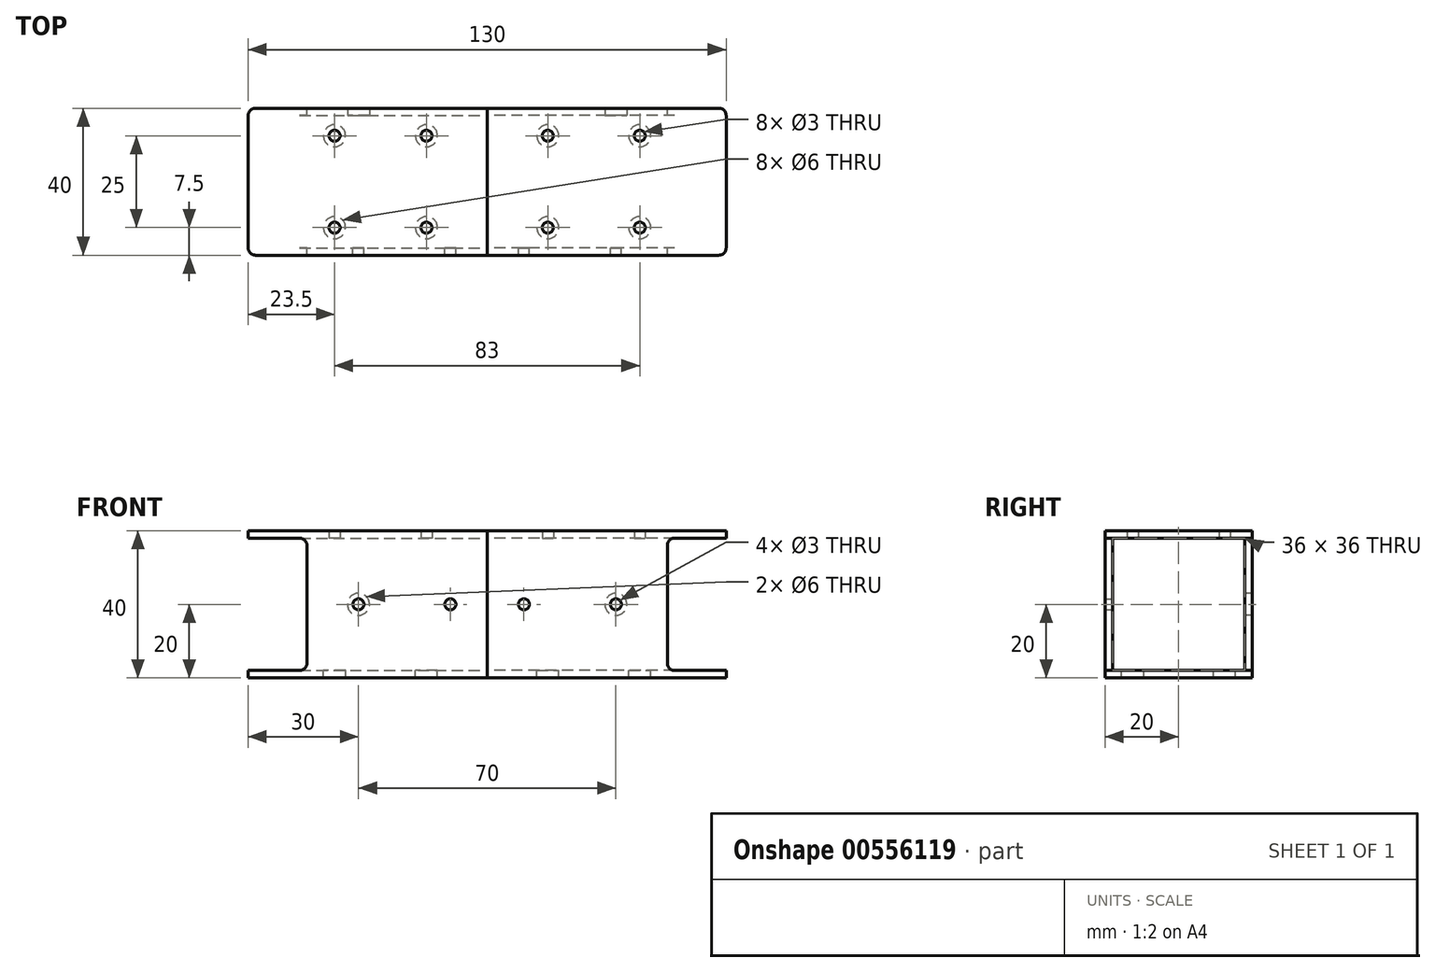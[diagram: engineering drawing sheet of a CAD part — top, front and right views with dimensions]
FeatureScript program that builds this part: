
annotation { "Feature Type Name" : "Feature", "Feature Type Description" : "" }
export const myFeature = defineFeature(function(context is Context, id is Id, definition is map)
    precondition{}
    {
        {
            var Q0;
            Q0=qCreatedBy(makeId("Right.planeOp"),FACE);
            var sketch = newSketch(context, id + "F0", { "sketchPlane" : qUnion([Q0])});
            skLineSegment(sketch, "E0.bottom", {"start": v(20, 20) * mm, "end": v(-20, 20) * mm});
            skLineSegment(sketch, "E0.top", {"start": v(20, -20) * mm, "end": v(-20, -20) * mm});
            skLineSegment(sketch, "E0.left", {"start": v(20, 20) * mm, "end": v(20, -20) * mm});
            skLineSegment(sketch, "E0.right", {"start": v(-20, 20) * mm, "end": v(-20, -20) * mm});
            skPoint(sketch, "E0.middle", {"position": v(0, 0) * mm});
            skSolve(sketch);
        }
        {
            var Q0;
            Q0=qSketchRegion(id+"F0",true);
            extrude(context, id + "F1", {"entities" : qUnion([Q0]), "oppositeDirection" : true, "depth" : 65 * mm, "offsetDistance" : 25 * mm});
        }
        {
            var Q0;
            Q0=makeQuery(id+"F1.opExtrude","CAP_FACE",FACE,{"disambiguationData":[OSD([sQuery(id+"F0.wireOp",EDGE,"E0.bottom"),sQuery(id+"F0.wireOp",EDGE,"E0.top"),sQuery(id+"F0.wireOp",EDGE,"E0.left"),sQuery(id+"F0.wireOp",EDGE,"E0.right")])],"isStart":false});
            var Q1;
            Q1=makeQuery(id+"F1.opExtrude","CAP_FACE",FACE,{"disambiguationData":[OSD([sQuery(id+"F0.wireOp",EDGE,"E0.bottom"),sQuery(id+"F0.wireOp",EDGE,"E0.top"),sQuery(id+"F0.wireOp",EDGE,"E0.left"),sQuery(id+"F0.wireOp",EDGE,"E0.right")])],"isStart":true});
            shell(context, id + "F2", {"entities" : qUnion([Q0, Q1]), "thickness" : 2 * mm});
        }
        {
            var Q0;
            Q0=makeQuery(id+"F2.opShell","OFFSET_FACE",FACE,{"disambiguationData":[OSD([sQuery(id+"F0.wireOp",EDGE,"E0.top")])]});
            var sketch = newSketch(context, id + "F3", { "sketchPlane" : qUnion([Q0])});
            skLineSegment(sketch, "E1", {"start": v(-65, 0) * mm, "end": v(0, 0) * mm, "construction": true});
            skLineSegment(sketch, "E2.bottom", {"start": v(-16.5, 12.5) * mm, "end": v(-41.5, 12.5) * mm, "construction": true});
            skLineSegment(sketch, "E2.top", {"start": v(-16.5, -12.5) * mm, "end": v(-41.5, -12.5) * mm, "construction": true});
            skLineSegment(sketch, "E2.left", {"start": v(-16.5, 12.5) * mm, "end": v(-16.5, -12.5) * mm, "construction": true});
            skLineSegment(sketch, "E2.right", {"start": v(-41.5, 12.5) * mm, "end": v(-41.5, -12.5) * mm, "construction": true});
            skPoint(sketch, "E2.middle", {"position": v(-29, 0) * mm});
            skLineSegment(sketch, "E3", {"start": v(-45, 18) * mm, "end": v(-45, -18) * mm, "construction": true});
            skSolve(sketch);
        }
        {
            var Q0;
            Q0=sQuery(id+"F3.wireOp",VERTEX,"E2.right.start");
            var Q1;
            Q1=sQuery(id+"F3.wireOp",VERTEX,"E2.bottom.start");
            var Q2;
            Q2=sQuery(id+"F3.wireOp",VERTEX,"E2.top.end");
            var Q3;
            Q3=sQuery(id+"F3.wireOp",VERTEX,"E2.left.end");
            var Q4;
            Q4=makeQuery(id+"F1.opExtrude","SWEPT_BODY",BODY,{"disambiguationData":[OSD([sQuery(id+"F0.wireOp",EDGE,"E0.bottom"),sQuery(id+"F0.wireOp",EDGE,"E0.top"),sQuery(id+"F0.wireOp",EDGE,"E0.left"),sQuery(id+"F0.wireOp",EDGE,"E0.right")])]});
            hole(context, id + "F4", {"style" : HoleStyle.SIMPLE, "endStyle" : HoleEndStyle.BLIND, "oppositeDirection" : true, "holeDiameter" : 3 * mm, "majorDiameter" : 5 * mm, "holeDepth" : 40 * mm, "isTappedThrough" : true, "tappedDepth" : 12 * mm, "tapClearance" : 3, "locations" : qUnion([Q0, Q1, Q2, Q3]), "scope" : qUnion([Q4])});
        }
        {
            var Q0;
            Q0=sQuery(id+"F3.wireOp",VERTEX,"E2.right.start");
            var Q1;
            Q1=sQuery(id+"F3.wireOp",VERTEX,"E2.top.end");
            var Q2;
            Q2=sQuery(id+"F3.wireOp",VERTEX,"E2.left.end");
            var Q3;
            Q3=sQuery(id+"F3.wireOp",VERTEX,"E2.left.start");
            var Q4;
            Q4=makeQuery(id+"F1.opExtrude","SWEPT_BODY",BODY,{"disambiguationData":[OSD([sQuery(id+"F0.wireOp",EDGE,"E0.bottom"),sQuery(id+"F0.wireOp",EDGE,"E0.top"),sQuery(id+"F0.wireOp",EDGE,"E0.left"),sQuery(id+"F0.wireOp",EDGE,"E0.right")])]});
            hole(context, id + "F5", {"style" : HoleStyle.SIMPLE, "endStyle" : HoleEndStyle.BLIND, "holeDiameter" : 6 * mm, "majorDiameter" : 5 * mm, "holeDepth" : 3 * mm, "isTappedThrough" : true, "tappedDepth" : 12 * mm, "tapClearance" : 3, "startFromSketch" : true, "locations" : qUnion([Q0, Q1, Q2, Q3]), "scope" : qUnion([Q4])});
        }
        {
            var Q0;
            Q0=makeQuery(id+"F2.opShell","OFFSET_FACE",FACE,{"disambiguationData":[OSD([sQuery(id+"F0.wireOp",EDGE,"E0.right")])]});
            var sketch = newSketch(context, id + "F6", { "sketchPlane" : qUnion([Q0])});
            skLineSegment(sketch, "E4", {"start": v(45, -20) * mm, "end": v(45, 20) * mm, "construction": true});
            skLineSegment(sketch, "E5", {"start": v(0, 0) * mm, "end": v(45, 0) * mm, "construction": true});
            skPoint(sketch, "E6", {"position": v(35, 0) * mm});
            skPoint(sketch, "E7", {"position": v(10, 0) * mm});
            skLineSegment(sketch, "E8.bottom", {"start": v(49, -18) * mm, "end": v(65, -18) * mm});
            skLineSegment(sketch, "E8.top", {"start": v(49, 18) * mm, "end": v(65, 18) * mm});
            skLineSegment(sketch, "E8.left", {"start": v(65, -18) * mm, "end": v(65, 18) * mm});
            skLineSegment(sketch, "E8.right", {"start": v(49, -18) * mm, "end": v(49, 18) * mm});
            skSolve(sketch);
        }
        {
            var Q0;
            Q0=makeQuery(id+"F6.imprint","IMPRINT",FACE,{"disambiguationData":[TD([[makeQuery(id+"F6.imprint","IMPRINT",EDGE,{"derivedFrom":sQuery(id+"F6.wireOp",EDGE,"E8.bottom")}),1.0]])]});
            var Q1;
            Q1=makeQuery(id+"F6.imprint","IMPRINT",FACE,{"disambiguationData":[TD([[makeQuery(id+"F6.imprint","IMPRINT",EDGE,{"derivedFrom":sQuery(id+"F6.wireOp",EDGE,"E8.bottom")}),-1.0]])]});
            extrude(context, id + "F7", {"entities" : qUnion([Q0, Q1]), "operationType" : NewBodyOperationType.REMOVE, "endBound" : BoundingType.THROUGH_ALL, "oppositeDirection" : true, "depth" : 25 * mm, "offsetDistance" : 25 * mm, "hasSecondDirection" : true, "secondDirectionBound" : SecondDirectionBoundingType.THROUGH_ALL, "secondDirectionOppositeDirection" : false, "secondDirectionDepth" : 25 * mm});
        }
        {
            var Q0;
            {var subQ0=sQuery(id+"F6.wireOp",EDGE,"E8.top");var subQ1=sQuery(id+"F0.wireOp",EDGE,"E0.right");var subQ2=sQuery(id+"F6.wireOp",EDGE,"E8.right");Q0=makeQuery(id+"F7.boolean.opBoolean","COPY",EDGE,{"disambiguationData":[TD([makeQuery(id+"F1.opExtrude","SWEPT_FACE",FACE,{"disambiguationData":[OSD([subQ1])]})])],"derivedFrom":makeQuery(id+"F7.opExtrude","SWEPT_EDGE",EDGE,{"disambiguationData":[OSD([subQ0,subQ2])]})});}
            var Q1;
            {var subQ0=sQuery(id+"F0.wireOp",EDGE,"E0.left");var subQ1=sQuery(id+"F6.wireOp",EDGE,"E8.top");var subQ2=sQuery(id+"F6.wireOp",EDGE,"E8.right");Q1=makeQuery(id+"F7.boolean.opBoolean","COPY",EDGE,{"disambiguationData":[TD([makeQuery(id+"F1.opExtrude","SWEPT_FACE",FACE,{"disambiguationData":[OSD([subQ0])]})])],"derivedFrom":makeQuery(id+"F7.opExtrude","SWEPT_EDGE",EDGE,{"disambiguationData":[OSD([subQ1,subQ2])]})});}
            var Q2;
            {var subQ0=sQuery(id+"F6.wireOp",EDGE,"E8.bottom");var subQ1=sQuery(id+"F0.wireOp",EDGE,"E0.left");var subQ2=sQuery(id+"F6.wireOp",EDGE,"E8.right");Q2=makeQuery(id+"F7.boolean.opBoolean","COPY",EDGE,{"disambiguationData":[TD([makeQuery(id+"F1.opExtrude","SWEPT_FACE",FACE,{"disambiguationData":[OSD([subQ1])]})])],"derivedFrom":makeQuery(id+"F7.opExtrude","SWEPT_EDGE",EDGE,{"disambiguationData":[OSD([subQ0,subQ2])]})});}
            var Q3;
            {var subQ0=sQuery(id+"F6.wireOp",EDGE,"E8.bottom");var subQ1=sQuery(id+"F0.wireOp",EDGE,"E0.right");var subQ2=sQuery(id+"F6.wireOp",EDGE,"E8.right");Q3=makeQuery(id+"F7.boolean.opBoolean","COPY",EDGE,{"disambiguationData":[TD([makeQuery(id+"F1.opExtrude","SWEPT_FACE",FACE,{"disambiguationData":[OSD([subQ1])]})])],"derivedFrom":makeQuery(id+"F7.opExtrude","SWEPT_EDGE",EDGE,{"disambiguationData":[OSD([subQ0,subQ2])]})});}
            var Q4;
            {var subQ0=sQuery(id+"F0.wireOp",EDGE,"E0.bottom");var subQ1=sQuery(id+"F0.wireOp",EDGE,"E0.left");Q4=makeQuery(id+"F7.boolean.opBoolean","SPLIT",EDGE,{"disambiguationData":[TD([makeQuery(id+"F1.opExtrude","SWEPT_FACE",FACE,{"disambiguationData":[OSD([subQ0])]})])],"derivedFrom":makeQuery(id+"F1.opExtrude","CAP_EDGE",EDGE,{"disambiguationData":[OSD([subQ1])],"isStart":false})});}
            var Q5;
            {var subQ0=sQuery(id+"F0.wireOp",EDGE,"E0.bottom");var subQ1=sQuery(id+"F0.wireOp",EDGE,"E0.right");Q5=makeQuery(id+"F7.boolean.opBoolean","SPLIT",EDGE,{"disambiguationData":[TD([makeQuery(id+"F1.opExtrude","SWEPT_FACE",FACE,{"disambiguationData":[OSD([subQ0])]})])],"derivedFrom":makeQuery(id+"F1.opExtrude","CAP_EDGE",EDGE,{"disambiguationData":[OSD([subQ1])],"isStart":false})});}
            var Q6;
            {var subQ0=sQuery(id+"F0.wireOp",EDGE,"E0.right");var subQ1=sQuery(id+"F0.wireOp",EDGE,"E0.top");Q6=makeQuery(id+"F7.boolean.opBoolean","SPLIT",EDGE,{"disambiguationData":[TD([makeQuery(id+"F1.opExtrude","SWEPT_FACE",FACE,{"disambiguationData":[OSD([subQ1])]})])],"derivedFrom":makeQuery(id+"F1.opExtrude","CAP_EDGE",EDGE,{"disambiguationData":[OSD([subQ0])],"isStart":false})});}
            var Q7;
            {var subQ0=sQuery(id+"F0.wireOp",EDGE,"E0.left");var subQ1=sQuery(id+"F0.wireOp",EDGE,"E0.top");Q7=makeQuery(id+"F7.boolean.opBoolean","SPLIT",EDGE,{"disambiguationData":[TD([makeQuery(id+"F1.opExtrude","SWEPT_FACE",FACE,{"disambiguationData":[OSD([subQ1])]})])],"derivedFrom":makeQuery(id+"F1.opExtrude","CAP_EDGE",EDGE,{"disambiguationData":[OSD([subQ0])],"isStart":false})});}
            fillet(context, id + "F8", {"entities" : qUnion([Q0, Q1, Q2, Q3, Q4, Q5, Q6, Q7]), "radius" : 2 * mm, "tangentPropagation" : true, "allowEdgeOverflow" : false});
        }
        {
            var Q0;
            Q0=sQuery(id+"F6.wireOp",VERTEX,"E6");
            var Q1;
            Q1=sQuery(id+"F6.wireOp",VERTEX,"E7");
            var Q2;
            Q2=makeQuery(id+"F1.opExtrude","SWEPT_BODY",BODY,{"disambiguationData":[OSD([sQuery(id+"F0.wireOp",EDGE,"E0.bottom"),sQuery(id+"F0.wireOp",EDGE,"E0.top"),sQuery(id+"F0.wireOp",EDGE,"E0.left"),sQuery(id+"F0.wireOp",EDGE,"E0.right")])]});
            hole(context, id + "F9", {"style" : HoleStyle.SIMPLE, "endStyle" : HoleEndStyle.BLIND, "holeDiameter" : 3 * mm, "majorDiameter" : 5 * mm, "holeDepth" : 3 * mm, "isTappedThrough" : true, "tappedDepth" : 12 * mm, "tapClearance" : 3, "startFromSketch" : true, "locations" : qUnion([Q0, Q1]), "scope" : qUnion([Q2])});
        }
        {
            var Q0;
            Q0=sQuery(id+"F6.wireOp",VERTEX,"E6");
            var Q1;
            Q1=makeQuery(id+"F1.opExtrude","SWEPT_BODY",BODY,{"disambiguationData":[OSD([sQuery(id+"F0.wireOp",EDGE,"E0.bottom"),sQuery(id+"F0.wireOp",EDGE,"E0.top"),sQuery(id+"F0.wireOp",EDGE,"E0.left"),sQuery(id+"F0.wireOp",EDGE,"E0.right")])]});
            hole(context, id + "F10", {"style" : HoleStyle.SIMPLE, "endStyle" : HoleEndStyle.BLIND, "oppositeDirection" : true, "holeDiameter" : 6 * mm, "majorDiameter" : 5 * mm, "holeDepth" : 40 * mm, "isTappedThrough" : true, "tappedDepth" : 12 * mm, "tapClearance" : 3, "startFromSketch" : true, "locations" : qUnion([Q0]), "scope" : qUnion([Q1])});
        }
        {
            var Q0;
            Q0=makeQuery(id+"F1.opExtrude","SWEPT_BODY",BODY,{"disambiguationData":[OSD([sQuery(id+"F0.wireOp",EDGE,"E0.bottom"),sQuery(id+"F0.wireOp",EDGE,"E0.top"),sQuery(id+"F0.wireOp",EDGE,"E0.left"),sQuery(id+"F0.wireOp",EDGE,"E0.right")])]});
            var Q1;
            Q1=qCreatedBy(makeId("Right.planeOp"),FACE);
            mirror(context, id + "F11", {"entities" : qUnion([Q0]), "mirrorPlane" : qUnion([Q1])});
        }
    });
